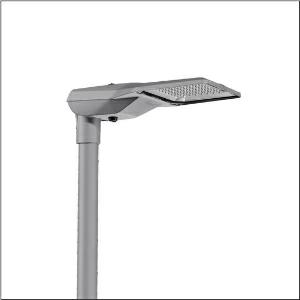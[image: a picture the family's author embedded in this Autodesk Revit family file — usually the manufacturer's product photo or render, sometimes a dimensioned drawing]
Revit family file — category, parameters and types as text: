
# Revit family: streetlight_sl_21_iq_midi___st1_5a_5xe3p31y08mb_5967
name_source: partatom
category: Lighting Fixtures
units: mm (PartAtom-declared; Revit-internal decimal feet)

## family parameters
Cut with Voids When Loaded = No
Host = Face
Light Source = No
Part Type = Normal
Room Calculation Point = No
Round Connector Dimension = Use Diameter
Shared = No

## types (1)
- --- (1 x LED, 18020 lm, 129.3 W, 3000K)
    Apparent Load = 129 VA
    CIE Flux Codes = 22 53 95 100 100
    Color Rendering = 70
    Color Temperature = 3000K
    Default Elevation = 1800 mm
    Description = Streetlight SL 21 iQ midi, mast luminaire, primary light control with lens, of PMMA, primary optical cover: cover, of toughened safety glass, transparent, light distribution: ST1.5a, light emission: direct distribution, primary light characteristic: asymmetric, installation type: post-top, side-entry, LED, High Power LED, rated luminous flux: 18.020lm, luminous efficacy: 139lm/W, light colour: 730, colour temperature: 3000K, control: pre-setting: logarithmic dimming characteristic, Street-Remote, Auto-Match, Temp-Guard, Lumen-Switch, Night-Set, Smart-Wire, Light-Fading, Desk-Remote (wireless, voltage-free reading and setting of iQ features in the workshop via application-optimized NFC function/RFID function), optimised constant luminous flux control (CLO 2.0), mains connection: 230..240V, AC, 50/60Hz, start of lifetime: 129W, end of service life: 142W, reduction: 56W, luminaire housing, of diecast aluminium, powder-coated, Siteco® metallic grey (DB 702S), corrosivity category C5 mid according to DIN EN ISO 12944, please order mast flange separately, inclination adjustable: 0°, 5°, 10°, 15°, sealing non-destructively replaceable, multi-level sealing system, length: 644mm, width: 335mm, height: 110mm, mast flange for spigot size: 42mm (side-entry): 5XC10008XM4, 60/48mm (side-entry/post-top): 5XC10108XM2, 76/60mm (side-entry/post-top): 5XC10108XM1, Smart Interface below and above, protection rating (complete): IP66, insulation class (complete): insulation class II (safety insulation), certification: CE, ENEC, ENEC+, VDE, impact resistance: IK09, permissible operating ambient temperature for outdoor applications: -40..+50°C, standard-compliant lighting for roads and squares, packaging unit: 1 piece

Light Distribution: ST1.5a
    Height = 111 mm
    Lamp = 1 x LED
    Lamp Light Flux = 18020 lm
    Lamp Power = 129.3 W
    Lamp count = 1
    Length = 644 mm
    Luminous efficacy = 139 lm/W
    Manufacturer = Siteco
    ModVariant = No
    Model = 5XE3P31Y08MB
    Number of Poles = 1
    OnlyDefault = Yes
    Power Factor = 1
    Product Name = Streetlight SL 21 iQ midi | ST1.5a
    Product group = mast luminaire | pylon top
    ProductGroupID = 6100
    Protection Class = Protection class II
    Protection Degree = IP 66
    RLX_Detail_Level = 1
    RLX_Emergency_Light_Flux = 0 lm
    RLX_Emergency_Type = 0
    RLX_Emergency_Type_DB = No
    RlxData = <blob elided: 94733 chars, md5=e53ccc28>
    Socket = socket
    Standby Power = 0 W
    System Light Flux = 18021 lm
    System Power = 129 W
    Type Comments = factory setting: luminous flux: 100 % | dim-lin: 254 | 672 mA
    Type Image = l_1004304.jpg
    URL = http://relux.com
    VarID = @adj_080713
    Voltage = 0 V
    Weight = 0.00 kg
    Width = 336 mm

## geometry (parser evidence)
native form markers: Blend x4, Sweep x13
no freeform markers — native parametric forms only
